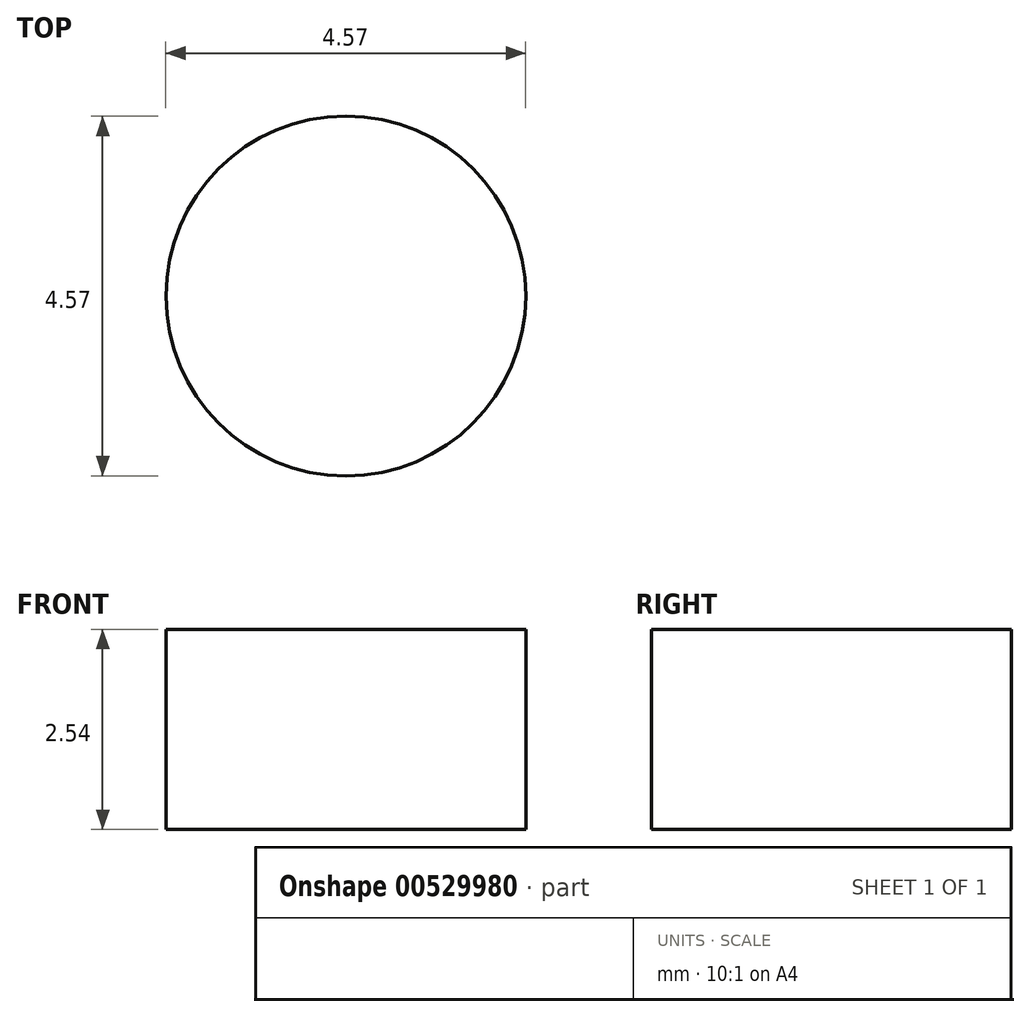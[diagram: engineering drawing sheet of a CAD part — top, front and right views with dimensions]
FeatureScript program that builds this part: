
annotation { "Feature Type Name" : "Feature", "Feature Type Description" : "" }
export const myFeature = defineFeature(function(context is Context, id is Id, definition is map)
    precondition{}
    {
        {
            var Q0;
            Q0=qCreatedBy(makeId("Top.planeOp"),FACE);
            var sketch = newSketch(context, id + "F0", { "sketchPlane" : qUnion([Q0])});
            skCircle(sketch, "E0", {"center": v(-38.97, 37.5) * mm, "radius": 2.29 * mm});
            skSolve(sketch);
        }
        {
            var Q0;
            Q0=makeQuery(id+"F0.imprint","IMPRINT",FACE,{"disambiguationData":[TD([[makeQuery(id+"F0.imprint","IMPRINT",EDGE,{"derivedFrom":sQuery(id+"F0.wireOp",EDGE,"E0")}),1.0]])]});
            extrude(context, id + "F1", {"entities" : qUnion([Q0]), "depth" : 2.54 * mm, "offsetDistance" : 25.4 * mm});
        }
    });
